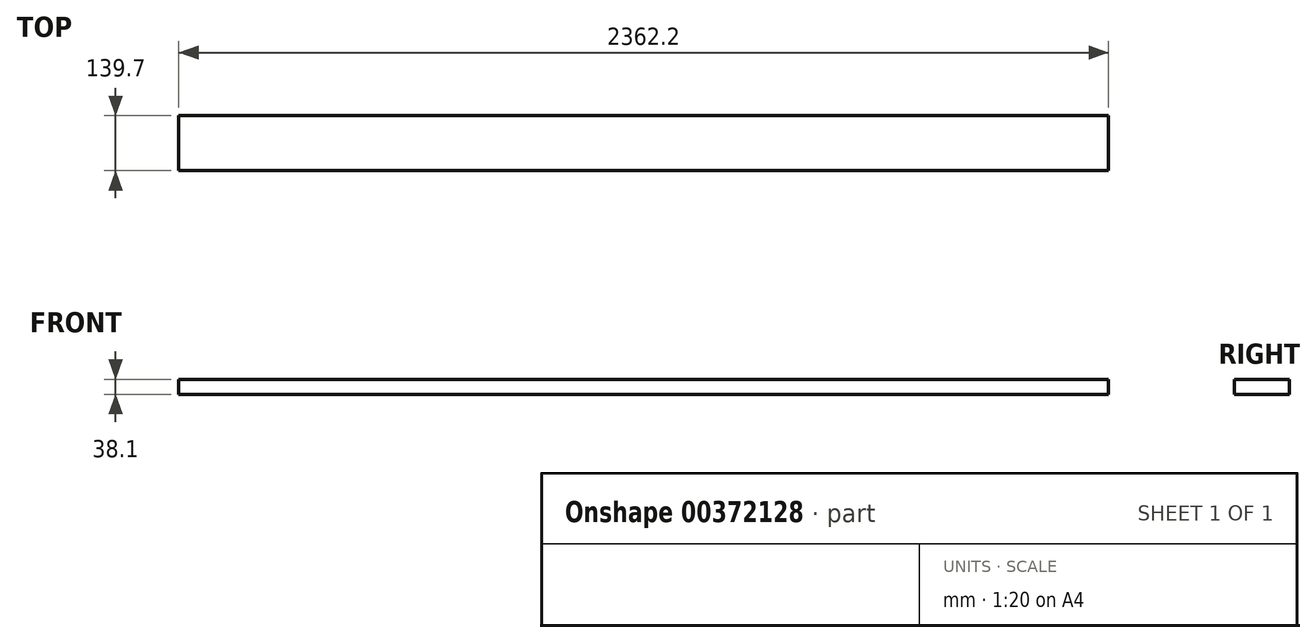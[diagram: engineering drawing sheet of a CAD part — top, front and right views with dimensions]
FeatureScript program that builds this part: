
annotation { "Feature Type Name" : "Feature", "Feature Type Description" : "" }
export const myFeature = defineFeature(function(context is Context, id is Id, definition is map)
    precondition{}
    {
        {
            var Q0;
            Q0=qCreatedBy(makeId("Top.planeOp"),FACE);
            var sketch = newSketch(context, id + "F0", { "sketchPlane" : qUnion([Q0])});
            skLineSegment(sketch, "E0.bottom", {"start": v(1181.1, -69.85) * mm, "end": v(-1181.1, -69.85) * mm});
            skLineSegment(sketch, "E0.top", {"start": v(1181.1, 69.85) * mm, "end": v(-1181.1, 69.85) * mm});
            skLineSegment(sketch, "E0.left", {"start": v(1181.1, -69.85) * mm, "end": v(1181.1, 69.85) * mm});
            skLineSegment(sketch, "E0.right", {"start": v(-1181.1, -69.85) * mm, "end": v(-1181.1, 69.85) * mm});
            skPoint(sketch, "E0.middle", {"position": v(0, 0) * mm});
            skSolve(sketch);
        }
        {
            var Q0;
            Q0=qSketchRegion(id+"F0",true);
            extrude(context, id + "F1", {"entities" : qUnion([Q0]), "oppositeDirection" : true, "depth" : 38.1 * mm});
        }
    });
